# Revit family: Bathtub-American_Standard-Studio-2938_Series
name_source: partatom
category: Plumbing Fixtures
revit_build: Autodesk Revit 2016 (Build: 20150714_1515(x64)
units: mm (PartAtom-declared; Revit-internal decimal feet)

## family parameters
Always vertical = No
Cut with Voids When Loaded = No
OmniClass Number = 23.45.05.14.21
OmniClass Title = Bathtubs
Part Type = Normal
Room Calculation Point = No
Round Connector Dimension = Use Diameter
Shared = Yes
Work Plane-Based = Yes

## types (3) — shared parameters
Assembly Code = D2010510
CW Connection = Yes
CWFU = 3
Default Elevation = 0"
Finish = Acrylic-American Standard-020-White
HW Connection = Yes
HWFU = 3
Height = 22 1/2"
Installation Type = Deck Mounted
Manufacturer = American Standard
Material = Acrylic-American Standard-020-White
Price = Prices may vary. Please consult Manufacturer Representative for most up-to-date price list.
Product Documentation Link = https://www.americanstandard-us.com
Revised Date = 6/30/2020
URL = http://www.americanstandard-us.com
Vent Connection = No
WFU = 4
Warranty Information = 1 Year Limited
Waste Connection = Yes
Waste Connection Diameter = 1 1/2"
Waste Connection Radius = 3/4"

## per-type parameters (varying)
| type | 2" Profile | 4" Profile | Deck Height | Description | Length | Product Page URL | Width | Zero-Edge Profile |
| 2938.002-D2.020 | Yes | No | 2" | Studio 65 3/4" Inch by 35 3/4" Inch Bathtub | 65 3/4" | https://www.americanstandard-us.com | 35 3/4" | No |
| 2938.002-D0.020 | No | No | 5/8" | Studio 66 Inch by 35 1/2 Inch Bathtub | 65 1/2" | https://www.americanstandard.ca | 35 1/2" | Yes |
| 2938.002-D4.020 | No | Yes | 4" | Studio 66 Inch by 36 Inch Bathtub | 66" | https://www.americanstandard-us.com | 36" | No |

note: column(s) folded — value = type name in every type: Model

## geometry (parser evidence)
native form markers: Sweep x2
no freeform markers — native parametric forms only
